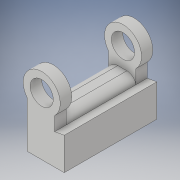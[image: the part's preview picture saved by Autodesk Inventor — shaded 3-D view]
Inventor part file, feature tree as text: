
AUTODESK INVENTOR PART (.ipt)
format: ipt  version: 2019 (Build 230136000, 136)  size: 170,496 bytes
history: native  units: in
note: dims shown in document units (in); Inventor stores cm internally (conversion verified against a paired STEP export)
features: sketch x7, extrude x5, fillet x2
ambient origin geometry x8: Origin, YZ Plane, XZ Plane, XY Plane, X Axis, Y Axis, Z Axis, Center Point
bodies: Solid1 (feature_tree)
feature tree (14):
  extrude  "Extrusion1"  Depth=0.315in
  sketch  "3D Sketch1"
  sketch  "Sketch2"  dims[d5=0.3937in d6=0.7874in d7=0.0in]
  extrude  "Extrusion2"  Depth=0.7874in TaperAngle=0.0deg
  extrude  "Extrusion3"  Depth=0.7874in TaperAngle=0.0deg
  extrude  "Extrusion4"  Depth=0.5935in
  fillet  "Fillet1"  Radius=0.3937in
  fillet  "Fillet2"  Radius=0.2756in
  extrude  "Extrusion5"  Depth=0.315in
  sketch  "Sketch1"  dims[d2=0.315in d3=0.1969in]
  sketch  "Sketch3"  dims[d8=0.7874in d9=0.0in d10=0.0039in d11=0.0in]
  sketch  "Sketch4"  dims[d12=0.315in d13=0.5935in d14=0.3937in d15=0.0in d17=0.2756in]
  sketch  "Sketch5"  dims[d18=0.1181in d19=0.315in]
  sketch  "Sketch6"  dims[d23=0.0787in d24=0.0787in d27=0.3937in d28=0.0in]
